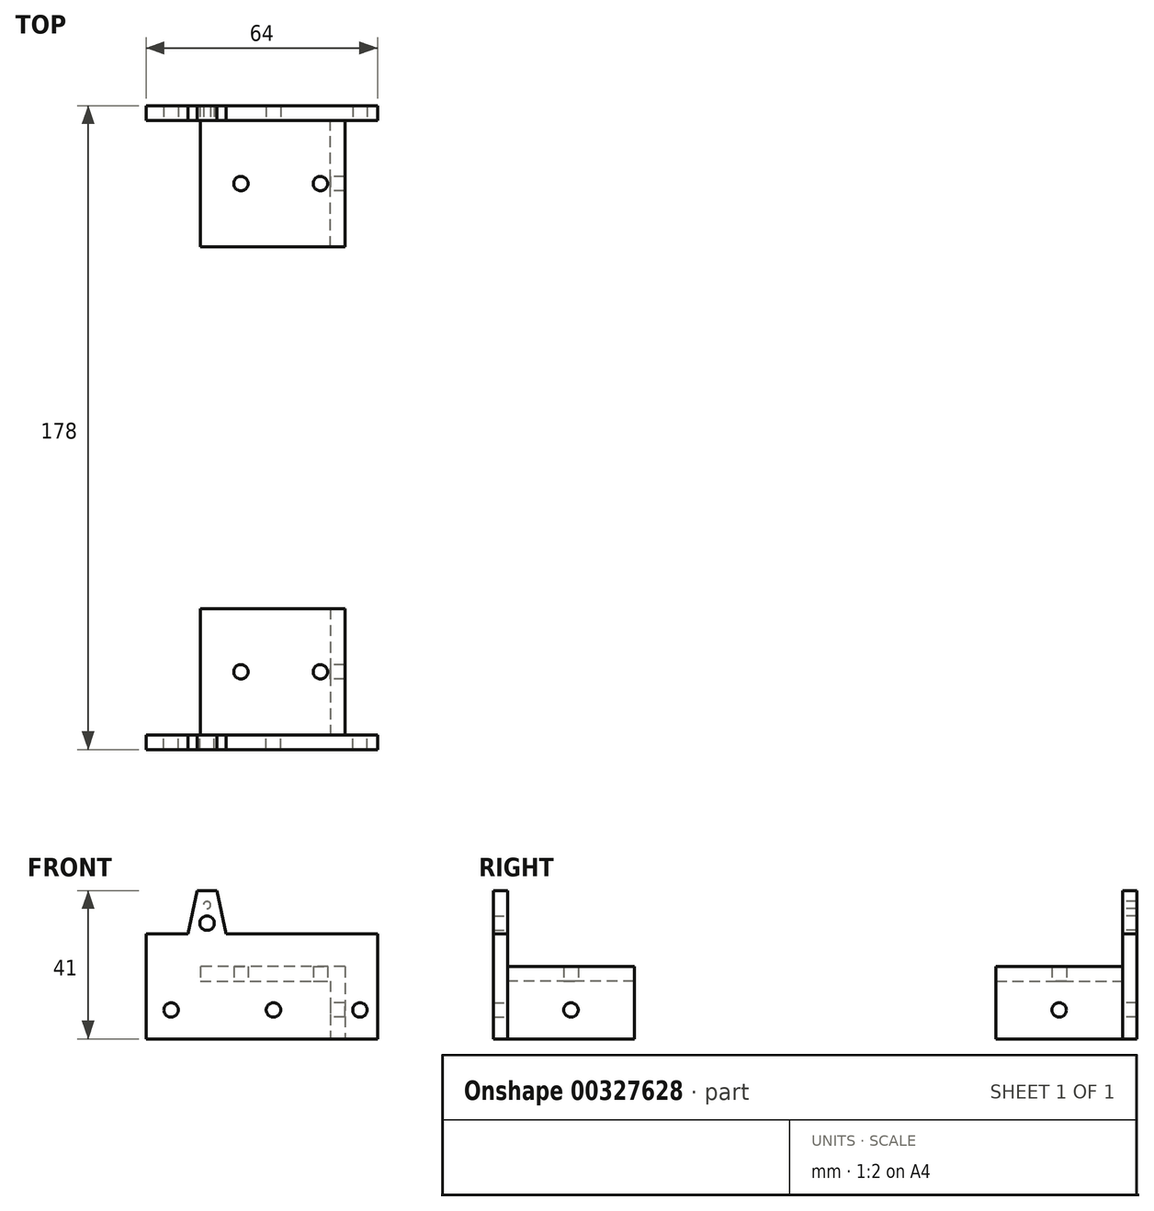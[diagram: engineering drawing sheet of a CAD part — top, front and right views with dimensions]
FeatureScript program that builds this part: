
annotation { "Feature Type Name" : "Feature", "Feature Type Description" : "" }
export const myFeature = defineFeature(function(context is Context, id is Id, definition is map)
    precondition{}
    {
        {
            assignVariable(context, id + "F0", {"name" : "P", "anyValue" : 4 * mm});
        }
        {
            var Q0;
            Q0=qCreatedBy(makeId("Front.planeOp"),FACE);
            var sketch = newSketch(context, id + "F1", { "sketchPlane" : qUnion([Q0])});
            skLineSegment(sketch, "E0", {"start": v(0, 0) * mm, "end": v(-40, 0) * mm});
            skLineSegment(sketch, "E1", {"start": v(0, 0) * mm, "end": v(0, -20) * mm});
            skLineSegment(sketch, "E2", {"start": v(0, -20) * mm, "end": v(-4, -20) * mm});
            skLineSegment(sketch, "E3", {"start": v(-40, 0) * mm, "end": v(-40, -4) * mm});
            skLineSegment(sketch, "E4", {"start": v(-40, -4) * mm, "end": v(-4, -4) * mm});
            skLineSegment(sketch, "E5", {"start": v(-4, -4) * mm, "end": v(-4, -20) * mm});
            skLineSegment(sketch, "E6", {"start": v(-55, 0) * mm, "end": v(-55, 9) * mm});
            skLineSegment(sketch, "E7", {"start": v(-55, 0) * mm, "end": v(-55, -20) * mm});
            skLineSegment(sketch, "E8", {"start": v(-55, 9) * mm, "end": v(9, 9) * mm});
            skLineSegment(sketch, "E9", {"start": v(9, 9) * mm, "end": v(9, -20) * mm});
            skLineSegment(sketch, "E10", {"start": v(9, -20) * mm, "end": v(-55, -20) * mm});
            skLineSegment(sketch, "E11", {"start": v(-55, 5) * mm, "end": v(9, 5) * mm, "construction": true});
            skLineSegment(sketch, "E12", {"start": v(5, 9) * mm, "end": v(5, -20) * mm, "construction": true});
            skPoint(sketch, "E13", {"position": v(-2, 5) * mm});
            skPoint(sketch, "E14", {"position": v(-6, 5) * mm});
            skPoint(sketch, "E15", {"position": v(-50, 5) * mm});
            skPoint(sketch, "E16", {"position": v(5, 2) * mm});
            skPoint(sketch, "E17", {"position": v(5, 6) * mm});
            skPoint(sketch, "E18", {"position": v(-19.75, -12) * mm});
            skPoint(sketch, "E18.positionSnap0", {"position": v(-4, -12) * mm});
            skPoint(sketch, "E19", {"position": v(-48.07, -12) * mm});
            skPoint(sketch, "E20", {"position": v(4.15, -12) * mm});
            skPoint(sketch, "E21", {"position": v(5, -2) * mm});
            skPoint(sketch, "E22", {"position": v(-10, 5) * mm});
            skLineSegment(sketch, "E23", {"start": v(-43.44, 9) * mm, "end": v(-40.8, 21) * mm});
            skLineSegment(sketch, "E24", {"start": v(-40.8, 21) * mm, "end": v(-35.44, 21) * mm});
            skLineSegment(sketch, "E25", {"start": v(-38.12, 21) * mm, "end": v(-38.12, 9) * mm, "construction": true});
            skLineSegment(sketch, "E26.MirrorCS", {"start": v(-32.8, 9) * mm, "end": v(-35.44, 21) * mm});
            skPoint(sketch, "E27", {"position": v(-38.12, 17) * mm});
            skPoint(sketch, "E28", {"position": v(-38.12, 12) * mm});
            skSolve(sketch);
        }
        {
            var Q0;
            Q0=makeQuery(id+"F1.imprint","IMPRINT",FACE,{"disambiguationData":[TD([[makeQuery(id+"F1.imprint","IMPRINT",EDGE,{"derivedFrom":sQuery(id+"F1.wireOp",EDGE,"E0")}),-1.0]])]});
            var Q1;
            Q1=makeQuery(id+"F1.imprint","IMPRINT",FACE,{"disambiguationData":[TD([[makeQuery(id+"F1.imprint","IMPRINT",EDGE,{"derivedFrom":sQuery(id+"F1.wireOp",EDGE,"E0")}),1.0]])]});
            var Q2;
            {var subQ0=sQuery(id+"F1.wireOp",EDGE,"E23");Q2=makeQuery(id+"F1.imprint","IMPRINT",FACE,{"disambiguationData":[TD([[makeQuery(id+"F1.imprint","IMPRINT",EDGE,{"derivedFrom":subQ0}),-1.0]])]});}
            extrude(context, id + "F2", {"entities" : qUnion([Q0, Q1, Q2]), "oppositeDirection" : true, "depth" : getVariable(context, 'P')});
        }
        {
            var Q0;
            Q0=makeQuery(id+"F1.imprint","IMPRINT",FACE,{"disambiguationData":[TD([[makeQuery(id+"F1.imprint","IMPRINT",EDGE,{"derivedFrom":sQuery(id+"F1.wireOp",EDGE,"E0")}),-1.0]])]});
            var sketch = newSketch(context, id + "F3", { "sketchPlane" : qUnion([Q0])});
            skPoint(sketch, "E29.0", {"position": v(-50, 5) * mm});
            skPoint(sketch, "E30.0", {"position": v(-6, 5) * mm});
            skPoint(sketch, "E31.0", {"position": v(-2, 5) * mm});
            skPoint(sketch, "E32.0", {"position": v(5, 6) * mm});
            skPoint(sketch, "E33.0", {"position": v(5, 2) * mm});
            skLineSegment(sketch, "E34.0", {"start": v(-55, 9) * mm, "end": v(9, 9) * mm});
            skLineSegment(sketch, "E35.0", {"start": v(9, 9) * mm, "end": v(9, -20) * mm});
            skLineSegment(sketch, "E36", {"start": v(-50, 5) * mm, "end": v(-50, 9) * mm});
            skLineSegment(sketch, "E37", {"start": v(-52, 9) * mm, "end": v(-52, 5) * mm});
            skArc(sketch, "E38", {"start": v(-52, 5) * mm, "mid": v(-51, 4) * mm, "end": v(-50, 5) * mm});
            skLineSegment(sketch, "E39", {"start": v(-2, 5) * mm, "end": v(-2, 9) * mm});
            skLineSegment(sketch, "E40", {"start": v(-4, 9) * mm, "end": v(-4, 5) * mm});
            skArc(sketch, "E41", {"start": v(-4, 5) * mm, "mid": v(-3, 4) * mm, "end": v(-2, 5) * mm});
            skLineSegment(sketch, "E42", {"start": v(-6, 5) * mm, "end": v(-6, 9) * mm});
            skLineSegment(sketch, "E43", {"start": v(-8, 9) * mm, "end": v(-8, 5) * mm});
            skArc(sketch, "E44", {"start": v(-8, 5) * mm, "mid": v(-7, 4) * mm, "end": v(-6, 5) * mm});
            skLineSegment(sketch, "E45", {"start": v(5, 2) * mm, "end": v(9, 2) * mm});
            skLineSegment(sketch, "E46", {"start": v(9, 4) * mm, "end": v(5, 4) * mm});
            skArc(sketch, "E47", {"start": v(5, 4) * mm, "mid": v(4, 3) * mm, "end": v(5, 2) * mm});
            skLineSegment(sketch, "E48", {"start": v(5, 6) * mm, "end": v(9, 6) * mm});
            skLineSegment(sketch, "E49", {"start": v(9, 8) * mm, "end": v(5, 8) * mm});
            skArc(sketch, "E50", {"start": v(5, 8) * mm, "mid": v(4, 7) * mm, "end": v(5, 6) * mm});
            skPoint(sketch, "E51.0", {"position": v(-10, 5) * mm});
            skPoint(sketch, "E52.0", {"position": v(5, -2) * mm});
            skLineSegment(sketch, "E53", {"start": v(5, -2) * mm, "end": v(9, -2) * mm});
            skLineSegment(sketch, "E54", {"start": v(9, 0) * mm, "end": v(5, 0) * mm});
            skArc(sketch, "E55", {"start": v(5, 0) * mm, "mid": v(4, -1) * mm, "end": v(5, -2) * mm});
            skLineSegment(sketch, "E56", {"start": v(-10, 5) * mm, "end": v(-10, 9) * mm});
            skLineSegment(sketch, "E57", {"start": v(-12, 9) * mm, "end": v(-12, 5) * mm});
            skArc(sketch, "E58", {"start": v(-12, 5) * mm, "mid": v(-11, 4) * mm, "end": v(-10, 5) * mm});
            skSolve(sketch);
        }
        {
            var Q0;
            Q0=makeQuery(id+"F1.imprint","IMPRINT",FACE,{"disambiguationData":[TD([[makeQuery(id+"F1.imprint","IMPRINT",EDGE,{"derivedFrom":sQuery(id+"F1.wireOp",EDGE,"E0")}),1.0]])]});
            extrude(context, id + "F4", {"entities" : qUnion([Q0]), "operationType" : NewBodyOperationType.ADD, "depth" : 35 * mm});
        }
        {
            var Q0;
            Q0=makeQuery(id+"F4.opExtrude","SWEPT_FACE",FACE,{"disambiguationData":[OSD([sQuery(id+"F1.wireOp",EDGE,"E4")])]});
            var sketch = newSketch(context, id + "F5", { "sketchPlane" : qUnion([Q0])});
            skLineSegment(sketch, "E59", {"start": v(-28.75, 17.5) * mm, "end": v(-6.8, 17.5) * mm, "construction": true});
            skPoint(sketch, "E59.startSnap0", {"position": v(-40, 17.5) * mm});
            skSolve(sketch);
        }
        {
            var Q0;
            Q0=makeQuery(id+"F4.opExtrude","SWEPT_FACE",FACE,{"disambiguationData":[OSD([sQuery(id+"F1.wireOp",EDGE,"E5")])]});
            var sketch = newSketch(context, id + "F6", { "sketchPlane" : qUnion([Q0])});
            skPoint(sketch, "E60", {"position": v(17.5, -12) * mm});
            skPoint(sketch, "E60.positionSnap0", {"position": v(35, -12) * mm});
            skPoint(sketch, "E60.positionSnap1", {"position": v(17.5, -20) * mm});
            skSolve(sketch);
        }
        {
            var Q0;
            Q0=sQuery(id+"F1.wireOp",VERTEX,"E19");
            var Q1;
            Q1=sQuery(id+"F1.wireOp",VERTEX,"E18");
            var Q2;
            Q2=sQuery(id+"F1.wireOp",VERTEX,"E20");
            var Q3;
            Q3=sQuery(id+"F6.wireOp",VERTEX,"E60");
            var Q4;
            Q4=sQuery(id+"F5.wireOp",VERTEX,"E59.end");
            var Q5;
            Q5=sQuery(id+"F5.wireOp",VERTEX,"E59.start");
            var Q6;
            Q6=sQuery(id+"F1.wireOp",VERTEX,"E28");
            var Q7;
            Q7=makeQuery(id+"F2.opExtrude","SWEPT_BODY",BODY,{"disambiguationData":[OSD([sQuery(id+"F1.wireOp",EDGE,"E6"),sQuery(id+"F1.wireOp",EDGE,"E7"),sQuery(id+"F1.wireOp",EDGE,"E8"),sQuery(id+"F1.wireOp",EDGE,"E9"),sQuery(id+"F1.wireOp",EDGE,"E10")])]});
            var Q8;
            Q8=makeQuery(id+"F4.opExtrude","SWEPT_BODY",BODY,{"disambiguationData":[OSD([sQuery(id+"F1.wireOp",EDGE,"E0"),sQuery(id+"F1.wireOp",EDGE,"E1"),sQuery(id+"F1.wireOp",EDGE,"E3"),sQuery(id+"F1.wireOp",EDGE,"E4"),sQuery(id+"F1.wireOp",EDGE,"E5"),sQuery(id+"F1.wireOp",EDGE,"E10")])]});
            hole(context, id + "F7", {"style" : HoleStyle.SIMPLE, "endStyle" : HoleEndStyle.THROUGH, "holeDiameter" : 4 * mm, "tappedDepth" : 12 * mm, "tapClearance" : 3, "locations" : qUnion([Q0, Q1, Q2, Q3, Q4, Q5, Q6]), "scope" : qUnion([Q7, Q8])});
        }
        {
            var Q0;
            Q0=makeQuery(id+"F2.opExtrude","CAP_FACE",FACE,{"disambiguationData":[OSD([sQuery(id+"F1.wireOp",EDGE,"E6"),sQuery(id+"F1.wireOp",EDGE,"E7"),sQuery(id+"F1.wireOp",EDGE,"E8"),sQuery(id+"F1.wireOp",EDGE,"E9"),sQuery(id+"F1.wireOp",EDGE,"E10")])],"isStart":false});
            var sketch = newSketch(context, id + "F8", { "sketchPlane" : qUnion([Q0])});
            skPoint(sketch, "E61", {"position": v(34.5, -11.96) * mm});
            skPoint(sketch, "E62", {"position": v(6, -11.96) * mm});
            skSolve(sketch);
        }
        {
            var Q0;
            Q0=makeQuery(id+"F4.opExtrude","CAP_FACE",FACE,{"disambiguationData":[OSD([sQuery(id+"F1.wireOp",EDGE,"E0"),sQuery(id+"F1.wireOp",EDGE,"E1"),sQuery(id+"F1.wireOp",EDGE,"E3"),sQuery(id+"F1.wireOp",EDGE,"E4"),sQuery(id+"F1.wireOp",EDGE,"E5"),sQuery(id+"F1.wireOp",EDGE,"E10")])],"isStart":false});
            cPlane(context, id + "F9", {"entities" : qUnion([Q0]), "cplaneType" : CPlaneType.OFFSET, "offset" : 50 * mm, "width" : 150 * mm, "height" : 150 * mm});
        }
        {
            var Q0;
            Q0=makeQuery(id+"F2.opExtrude","SWEPT_BODY",BODY,{"disambiguationData":[OSD([sQuery(id+"F1.wireOp",EDGE,"E6"),sQuery(id+"F1.wireOp",EDGE,"E7"),sQuery(id+"F1.wireOp",EDGE,"E8"),sQuery(id+"F1.wireOp",EDGE,"E9"),sQuery(id+"F1.wireOp",EDGE,"E10")])]});
            var Q1;
            Q1=qCreatedBy(id+"F9.planeOp",FACE);
            mirror(context, id + "F10", {"entities" : qUnion([Q0]), "mirrorPlane" : qUnion([Q1])});
        }
        {
            var Q0;
            Q0=sQuery(id+"F1.wireOp",VERTEX,"E27");
            var Q1;
            Q1=makeQuery(id+"F2.opExtrude","SWEPT_BODY",BODY,{"disambiguationData":[OSD([sQuery(id+"F1.wireOp",EDGE,"E6"),sQuery(id+"F1.wireOp",EDGE,"E7"),sQuery(id+"F1.wireOp",EDGE,"E8"),sQuery(id+"F1.wireOp",EDGE,"E9"),sQuery(id+"F1.wireOp",EDGE,"E10"),sQuery(id+"F1.wireOp",EDGE,"E23"),sQuery(id+"F1.wireOp",EDGE,"E24"),sQuery(id+"F1.wireOp",EDGE,"E26.MirrorCS")])]});
            hole(context, id + "F11", {"style" : HoleStyle.SIMPLE, "endStyle" : HoleEndStyle.THROUGH, "holeDiameter" : 2 * mm, "tappedDepth" : 12 * mm, "tapClearance" : 3, "locations" : qUnion([Q0]), "scope" : qUnion([Q1])});
        }
    });
